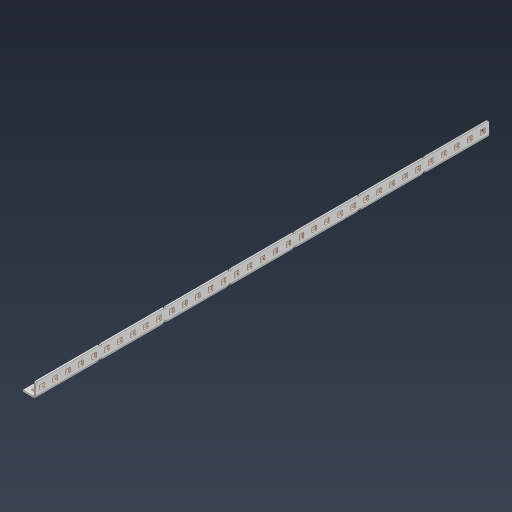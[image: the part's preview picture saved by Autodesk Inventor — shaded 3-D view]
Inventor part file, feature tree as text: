
AUTODESK INVENTOR PART (.ipt)
format: ipt  version: 2024.3 (Build 283343000, 343)  size: 1,248,256 bytes
history: native  units: in
note: dims shown in document units (in); Inventor stores cm internally (conversion verified against a paired STEP export)
features: other x111, extrude x102, sheet_metal_op x11, pattern_linear x2, mirror x1, chamfer x1, sketch x1
ambient origin geometry x8: Origin, YZ Plane, XZ Plane, XY Plane, X Axis, Y Axis, Z Axis, Center Point
bodies: Solid1 (feature_tree), Body (feature_tree)
feature tree (229):
  sheet_metal_op  "Flanges"
  other  "Flange Pattern Plane"
  other  "Flange Pattern Sketch"
  sheet_metal_op  "Flange Pattern"
  sheet_metal_op  "Body Pattern"
  pattern_linear  "Center Pattern"  Spacing1=17.5in  [1 undecoded]
  other  "Arc Length"
  mirror  "Notch Mirror"
  pattern_linear  "Notch Pattern"  Spacing1=0.0625in  [1 undecoded]
  chamfer  "End Chamfer"
  extrude  "Half Cut"  Depth=0.0625in
  other  "Plate1"
  sketch  "Sketch2"  dims[d0=1.0in d1=17.5in d2=0.0625in d3=0.0625in d4=0.0312in d5=0.125in d6=0.0625in d7=0.5in d8=90.0deg d9=0.0312in d10=0.25in d11=0.0625in d12=0.0625in d16=0.182in d17=0.02in d18=0.0625in d19=0.0in d20=0.25in d21=0.25in d38=13.7795in d40=0.5in d41=0.3937in d43=1.0in d46=0.172in d47=1.0in d48=0.0in d49=0.182in d50=0.02in d51=0.25in d52=0.25in d53=0.0625in d54=0.0in d55=0.172in d56=1.0in d57=0.0in d58=0.25in d60=13.7795in d62=0.5in d63=0.3937in d65=0.5in d85=0.1473in d86=0.1782in d88=0.04in d89=0.0625in d90=0.0in d91=0.04in d92=0.0491in d95=2.5in d96=0.04in d97=0.25in d98=45.0deg d99=0.25in d100=0.5in d101=0.0in d102=2.497in d106=0.182in d107=0.02in d108=0.5in d109=0.5in d110=0.0625in d111=0.0in d112=0.172in d113=0.5in d114=0.0in d117=0.5in d118=0.5in d119=0.5in]
  other  "Plate2"
  sheet_metal_op  "Bend1"
  sheet_metal_op  "Corner1"
  other  "Srf1"
  other  "Srf2"
  other  "Srf91"
  sheet_metal_op  "Body Pattern Sketch"
  other  "Srf92"
  other  "Srf786"
  other  "Srf823"
  other  "Srf824"
  other  "Srf825"
  other  "Srf826"
  other  "Srf827"
  other  "Srf828"
  other  "Srf829"
  other  "Srf856"
  other  "Srf857"
  other  "Srf858"
  other  "Srf859"
  other  "Srf860"
  other  "Srf861"
  other  "Srf862"
  other  "Srf889"
  other  "Srf890"
  other  "Srf891"
  other  "Srf892"
  other  "Srf893"
  other  "Srf894"
  other  "Srf895"
  other  "Srf896"
  other  "Srf1275"
  other  "Srf1276"
  other  "Srf1277"
  other  "Srf1278"
  other  "Srf1279"
  other  "Srf1280"
  other  "Srf1281"
  other  "Srf1282"
  other  "Srf1283"
  other  "Srf1284"
  other  "Srf1285"
  other  "Srf1286"
  other  "Srf1287"
  other  "Srf1288"
  other  "Srf1289"
  other  "Srf1290"
  other  "Srf1291"
  other  "Srf1292"
  other  "Srf1293"
  other  "Srf1294"
  other  "Srf1295"
  other  "Srf1296"
  other  "Srf1297"
  other  "Srf1298"
  other  "Srf1299"
  other  "Srf1300"
  other  "Srf1301"
  other  "Srf1302"
  other  "Srf1303"
  other  "Srf1304"
  other  "Srf1305"
  other  "Srf1306"
  other  "Srf1307"
  other  "Srf1308"
  other  "Srf1309"
  other  "Srf1310"
  other  "Srf1311"
  other  "Srf1312"
  other  "Srf1313"
  other  "Srf1314"
  other  "Srf1315"
  other  "Srf1316"
  other  "Srf1317"
  other  "Srf1318"
  other  "Srf1319"
  other  "Srf1320"
  other  "Srf1321"
  other  "Srf1322"
  other  "Srf1323"
  other  "Srf1324"
  other  "Srf1325"
  other  "Srf1326"
  other  "Srf1327"
  other  "Srf1328"
  other  "Srf1329"
  other  "Srf1330"
  other  "Srf1331"
  other  "Srf1332"
  other  "Srf1333"
  other  "Srf1334"
  other  "Srf1335"
  other  "Srf1336"
  other  "Srf1337"
  other  "Srf1338"
  other  "Srf1339"
  other  "Srf1340"
  other  "Srf1341"
  other  "Srf1342"
  other  "Srf1343"
  other  "Srf1344"
  other  "Srf1345"
  other  "Srf1346"
  other  "Srf1347"
  other  "Srf1348"
  other  "Srf1349"
  other  "Srf1350"
  other  "Srf1351"
  sheet_metal_op  "Flange Stamp"
  sheet_metal_op  "Flange Circle"
  sheet_metal_op  "Body Stamp"
  sheet_metal_op  "Body Circle"
  other  "Center Stamp"
  other  "Center Circle"
  sheet_metal_op  "Notch"
  extrude  "ExtrusionSrf2"  Depth=0.0312in
  extrude  "ExtrusionSrf92"  Depth=0.5in
  extrude  "ExtrusionSrf823"  Depth=0.0625in
  extrude  "ExtrusionSrf824"  Depth=0.5in TaperAngle=90.0deg
  extrude  "ExtrusionSrf825"  Depth=0.25in
  extrude  "ExtrusionSrf826"  Depth=0.0625in
  extrude  "ExtrusionSrf827"  Depth=0.0625in
  extrude  "ExtrusionSrf828"  Depth=0.182in
  extrude  "ExtrusionSrf829"  Depth=0.02in
  extrude  "ExtrusionSrf856"  Depth=0.0625in
  extrude  "ExtrusionSrf857"  TaperAngle=0.0deg  [1 undecoded]
  extrude  "ExtrusionSrf858"  Depth=0.25in
  extrude  "ExtrusionSrf859"  Depth=0.25in
  extrude  "ExtrusionSrf860"  Depth=0.5in
  extrude  "ExtrusionSrf861"  Depth=0.5in
  extrude  "ExtrusionSrf862"  Depth=1.0in TaperAngle=0.0deg
  extrude  "ExtrusionSrf889"  Depth=0.182in
  extrude  "ExtrusionSrf890"  Depth=0.02in
  extrude  "ExtrusionSrf891"  Depth=0.25in
  extrude  "ExtrusionSrf892"  Depth=0.25in
  extrude  "ExtrusionSrf893"  Depth=0.0625in
  extrude  "ExtrusionSrf894"  TaperAngle=0.0deg  [1 undecoded]
  extrude  "ExtrusionSrf895"  Depth=0.5in
  extrude  "ExtrusionSrf896"  Depth=1.0in TaperAngle=0.0deg
  extrude  "ExtrusionSrf1275"  Depth=0.25in
  extrude  "ExtrusionSrf1276"  Depth=0.5in
  extrude  "ExtrusionSrf1277"  Depth=0.5in
  extrude  "ExtrusionSrf1278"  Depth=0.5in
  extrude  "ExtrusionSrf1279"  Depth=0.5in
  extrude  "ExtrusionSrf1280"  Depth=0.5in
  extrude  "ExtrusionSrf1281"  Depth=0.0625in
  extrude  "ExtrusionSrf1282"  TaperAngle=0.0deg  [1 undecoded]
  extrude  "ExtrusionSrf1283"  Depth=0.5in
  extrude  "ExtrusionSrf1284"  Depth=0.5in
  extrude  "ExtrusionSrf1285"  Depth=2.5in
  extrude  "ExtrusionSrf1286"  Depth=0.25in TaperAngle=45.0deg
  extrude  "ExtrusionSrf1287"  Depth=0.25in
  extrude  "ExtrusionSrf1288"  Depth=0.5in TaperAngle=0.0deg
  extrude  "ExtrusionSrf1289"  Depth=0.5in
  extrude  "ExtrusionSrf1290"  Depth=0.182in
  extrude  "ExtrusionSrf1291"  Depth=0.02in
  extrude  "ExtrusionSrf1292"  Depth=0.5in
  extrude  "ExtrusionSrf1293"  Depth=0.5in
  extrude  "ExtrusionSrf1294"  Depth=0.0625in
  extrude  "ExtrusionSrf1295"  TaperAngle=0.0deg  [1 undecoded]
  extrude  "ExtrusionSrf1296"  Depth=0.5in
  extrude  "ExtrusionSrf1297"  Depth=0.5in TaperAngle=0.0deg
  extrude  "ExtrusionSrf1298"  Depth=0.5in
  extrude  "ExtrusionSrf1299"  Depth=0.5in
  extrude  "ExtrusionSrf1300"  Depth=0.5in
  extrude  "ExtrusionSrf1301"  [1 undecoded]
  extrude  "ExtrusionSrf1302"  [1 undecoded]
  extrude  "ExtrusionSrf1303"  [1 undecoded]
  extrude  "ExtrusionSrf1304"  [1 undecoded]
  extrude  "ExtrusionSrf1305"  [1 undecoded]
  extrude  "ExtrusionSrf1306"  [1 undecoded]
  extrude  "ExtrusionSrf1307"  [1 undecoded]
  extrude  "ExtrusionSrf1308"  [1 undecoded]
  extrude  "ExtrusionSrf1309"  [1 undecoded]
  extrude  "ExtrusionSrf1310"  [1 undecoded]
  extrude  "ExtrusionSrf1311"  [1 undecoded]
  extrude  "ExtrusionSrf1312"  [1 undecoded]
  extrude  "ExtrusionSrf1313"  [1 undecoded]
  extrude  "ExtrusionSrf1314"  [1 undecoded]
  extrude  "ExtrusionSrf1315"  [1 undecoded]
  extrude  "ExtrusionSrf1316"  [1 undecoded]
  extrude  "ExtrusionSrf1317"  [1 undecoded]
  extrude  "ExtrusionSrf1318"  [1 undecoded]
  extrude  "ExtrusionSrf1319"  [1 undecoded]
  extrude  "ExtrusionSrf1320"  [1 undecoded]
  extrude  "ExtrusionSrf1321"  [1 undecoded]
  extrude  "ExtrusionSrf1322"  [1 undecoded]
  extrude  "ExtrusionSrf1323"  [1 undecoded]
  extrude  "ExtrusionSrf1324"  [1 undecoded]
  extrude  "ExtrusionSrf1325"  [1 undecoded]
  extrude  "ExtrusionSrf1326"  [1 undecoded]
  extrude  "ExtrusionSrf1327"  [1 undecoded]
  extrude  "ExtrusionSrf1328"  [1 undecoded]
  extrude  "ExtrusionSrf1329"  [1 undecoded]
  extrude  "ExtrusionSrf1330"  [1 undecoded]
  extrude  "ExtrusionSrf1331"  [1 undecoded]
  extrude  "ExtrusionSrf1332"  [1 undecoded]
  extrude  "ExtrusionSrf1333"  [1 undecoded]
  extrude  "ExtrusionSrf1334"  [1 undecoded]
  extrude  "ExtrusionSrf1335"  [1 undecoded]
  extrude  "ExtrusionSrf1336"  [1 undecoded]
  extrude  "ExtrusionSrf1337"  [1 undecoded]
  extrude  "ExtrusionSrf1338"  [1 undecoded]
  extrude  "ExtrusionSrf1339"  [1 undecoded]
  extrude  "ExtrusionSrf1340"  [1 undecoded]
  extrude  "ExtrusionSrf1341"  [1 undecoded]
  extrude  "ExtrusionSrf1342"  [1 undecoded]
  extrude  "ExtrusionSrf1343"  [1 undecoded]
  extrude  "ExtrusionSrf1344"  [1 undecoded]
  extrude  "ExtrusionSrf1345"  [1 undecoded]
  extrude  "ExtrusionSrf1346"  [1 undecoded]
  extrude  "ExtrusionSrf1347"  [1 undecoded]
  extrude  "ExtrusionSrf1348"  [1 undecoded]
  extrude  "ExtrusionSrf1349"  [1 undecoded]
  extrude  "ExtrusionSrf1350"  [1 undecoded]
  extrude  "ExtrusionSrf1351"  [1 undecoded]
note: 57 required parameter values undecoded (feature->parameter linkage not recoverable at this tier; creation-order binding heuristic only, values carry confidence <= 0.55)
